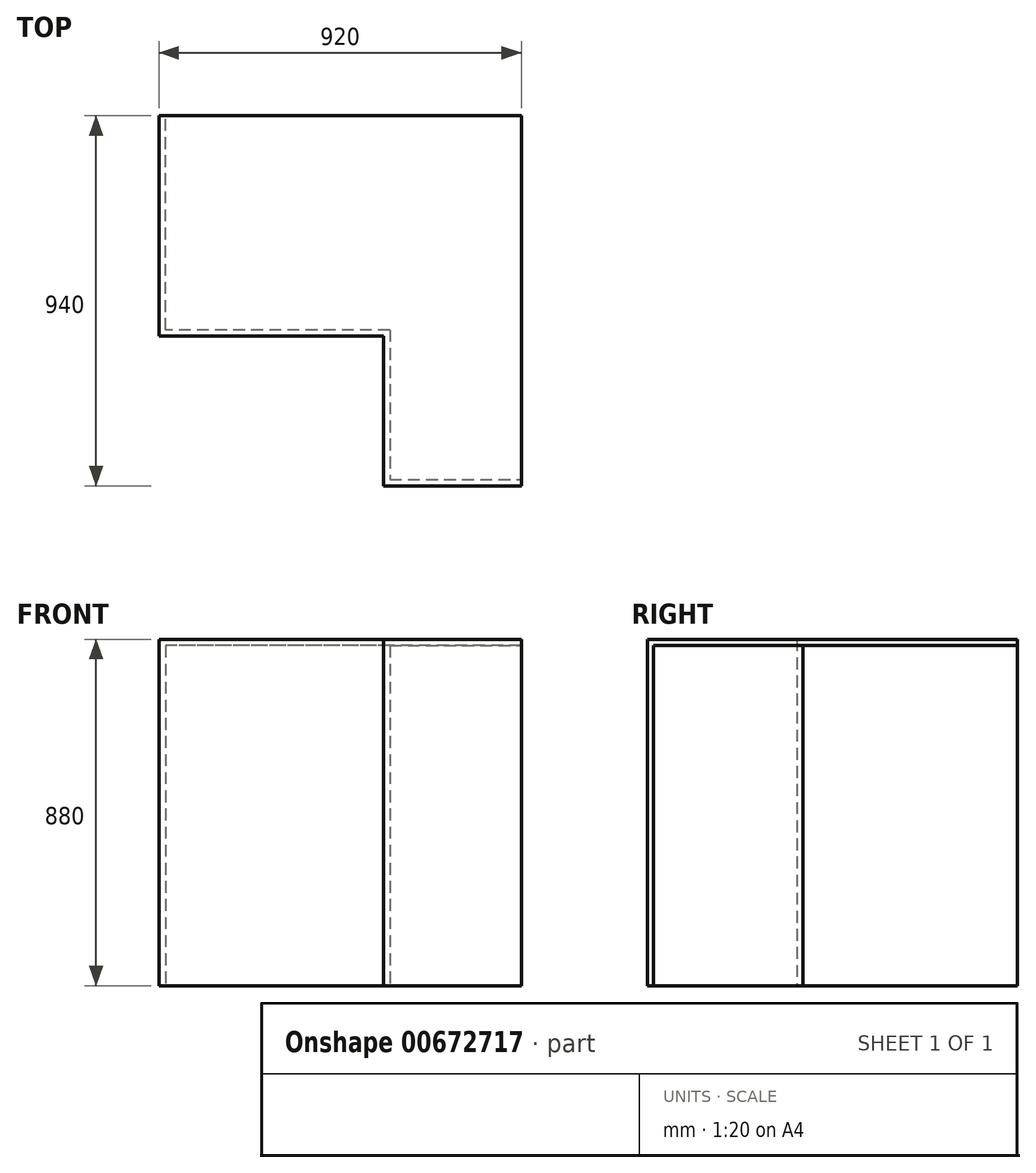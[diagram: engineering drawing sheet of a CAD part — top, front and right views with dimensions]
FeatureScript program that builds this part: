
annotation { "Feature Type Name" : "Feature", "Feature Type Description" : "" }
export const myFeature = defineFeature(function(context is Context, id is Id, definition is map)
    precondition{}
    {
        {
            var Q0;
            Q0=qCreatedBy(makeId("Top.planeOp"),FACE);
            var sketch = newSketch(context, id + "F0", { "sketchPlane" : qUnion([Q0])});
            skLineSegment(sketch, "E0.bottom", {"start": v(0, 0) * mm, "end": v(-570, 0) * mm});
            skLineSegment(sketch, "E0.top", {"start": v(350, 560) * mm, "end": v(-570, 560) * mm});
            skLineSegment(sketch, "E0.right", {"start": v(-570, 0) * mm, "end": v(-570, 560) * mm});
            skLineSegment(sketch, "E1.top", {"start": v(0, -380) * mm, "end": v(350, -380) * mm});
            skLineSegment(sketch, "E1.left", {"start": v(0, 0) * mm, "end": v(0, -380) * mm});
            skLineSegment(sketch, "E1.right", {"start": v(350, 560) * mm, "end": v(350, -380) * mm});
            skSolve(sketch);
        }
        {
            var Q0;
            Q0=makeQuery(id+"F0.imprint","IMPRINT",FACE,{"disambiguationData":[TD([[makeQuery(id+"F0.imprint","IMPRINT",EDGE,{"derivedFrom":sQuery(id+"F0.wireOp",EDGE,"E0.bottom")}),-1.0]])]});
            extrude(context, id + "F1", {"entities" : qUnion([Q0]), "depth" : 880 * mm, "offsetDistance" : 25 * mm});
        }
        {
            var Q0;
            Q0=makeQuery(id+"F1.opExtrude","SWEPT_FACE",FACE,{"disambiguationData":[OSD([sQuery(id+"F0.wireOp",EDGE,"E0.top")])]});
            var Q1;
            Q1=makeQuery(id+"F1.opExtrude","SWEPT_FACE",FACE,{"disambiguationData":[OSD([sQuery(id+"F0.wireOp",EDGE,"E1.right")])]});
            var Q2;
            Q2=makeQuery(id+"F1.opExtrude","CAP_FACE",FACE,{"disambiguationData":[OSD([sQuery(id+"F0.wireOp",EDGE,"E0.bottom"),sQuery(id+"F0.wireOp",EDGE,"E0.top"),sQuery(id+"F0.wireOp",EDGE,"E0.right"),sQuery(id+"F0.wireOp",EDGE,"E1.top"),sQuery(id+"F0.wireOp",EDGE,"E1.left"),sQuery(id+"F0.wireOp",EDGE,"E1.right")])],"isStart":true});
            shell(context, id + "F2", {"entities" : qUnion([Q0, Q1, Q2]), "thickness" : 16 * mm});
        }
    });
